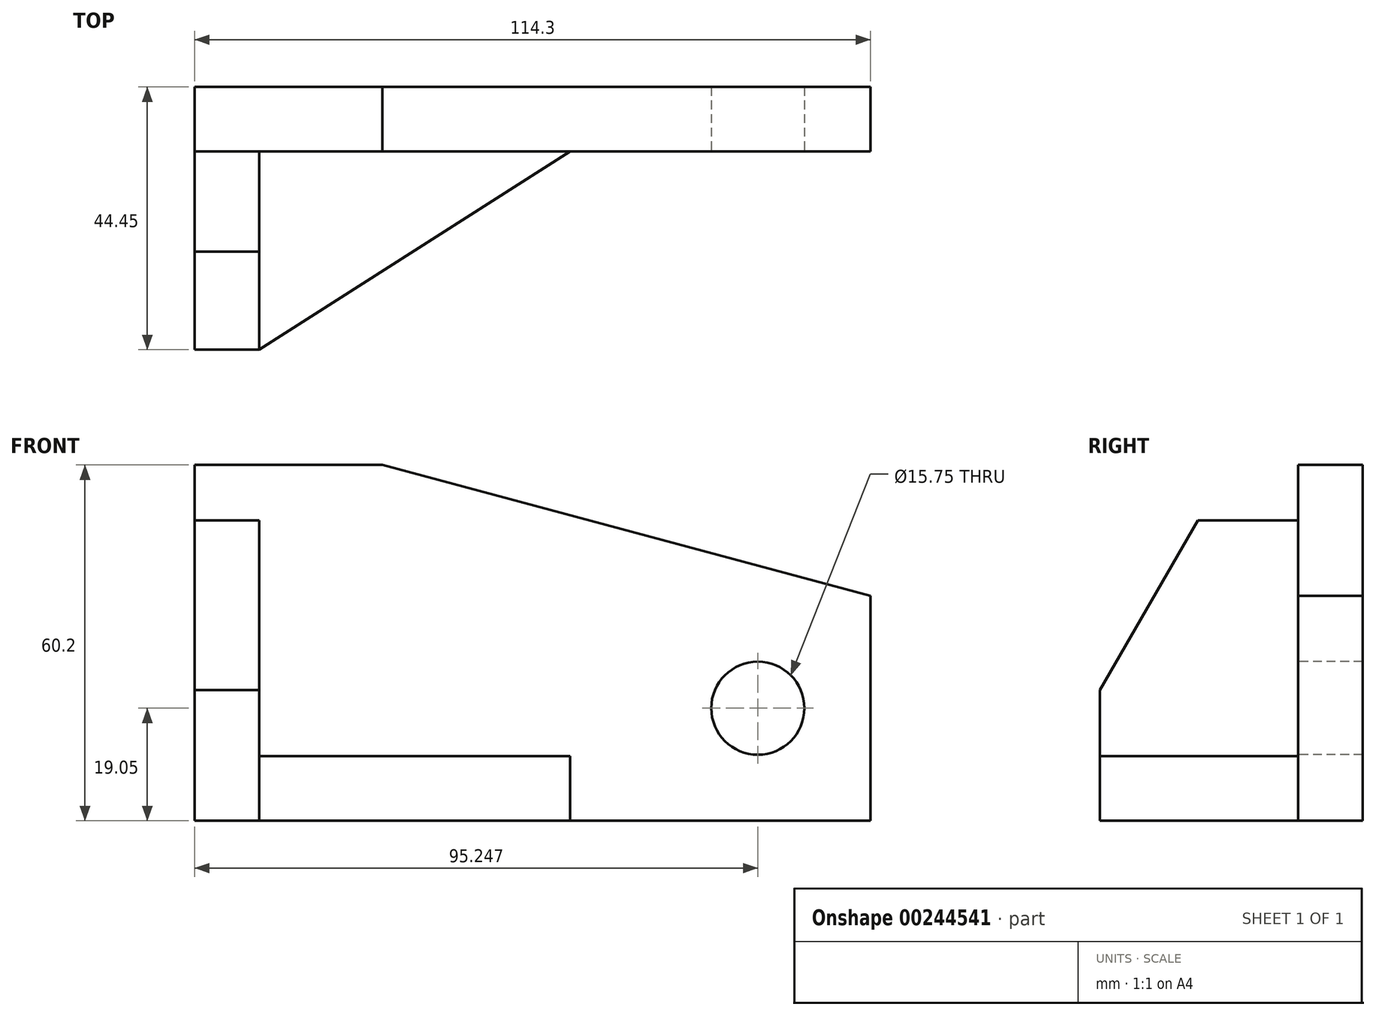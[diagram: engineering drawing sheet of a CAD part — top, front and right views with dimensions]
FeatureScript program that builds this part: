
annotation { "Feature Type Name" : "Feature", "Feature Type Description" : "" }
export const myFeature = defineFeature(function(context is Context, id is Id, definition is map)
    precondition{}
    {
        {
            var Q0;
            Q0=qCreatedBy(makeId("Top.planeOp"),FACE);
            var sketch = newSketch(context, id + "F0", { "sketchPlane" : qUnion([Q0])});
            skLineSegment(sketch, "E0", {"start": v(-76.4, -76.3) * mm, "end": v(-65.48, -76.3) * mm});
            skLineSegment(sketch, "E1", {"start": v(-76.4, -76.3) * mm, "end": v(-12.9, -76.3) * mm});
            skLineSegment(sketch, "E2", {"start": v(-76.4, -76.3) * mm, "end": v(-76.4, -42.77) * mm});
            skLineSegment(sketch, "E3", {"start": v(-76.4, -42.77) * mm, "end": v(-76.4, -31.85) * mm});
            skLineSegment(sketch, "E4", {"start": v(-65.48, -76.3) * mm, "end": v(-65.48, -42.77) * mm});
            skLineSegment(sketch, "E5", {"start": v(-65.48, -42.77) * mm, "end": v(-76.4, -42.77) * mm});
            skLineSegment(sketch, "E6", {"start": v(-65.48, -42.77) * mm, "end": v(-12.9, -42.77) * mm});
            skLineSegment(sketch, "E7", {"start": v(-12.9, -42.77) * mm, "end": v(-65.48, -76.3) * mm});
            skLineSegment(sketch, "E8", {"start": v(-76.4, -31.85) * mm, "end": v(37.9, -31.85) * mm});
            skLineSegment(sketch, "E9", {"start": v(-12.9, -42.77) * mm, "end": v(37.9, -42.77) * mm});
            skLineSegment(sketch, "E10", {"start": v(37.9, -42.77) * mm, "end": v(37.9, -31.85) * mm});
            skSolve(sketch);
        }
        {
            var Q0;
            Q0=makeQuery(id+"F0.imprint","IMPRINT",FACE,{"disambiguationData":[TD([[makeQuery(id+"F0.imprint","IMPRINT",EDGE,{"derivedFrom":sQuery(id+"F0.wireOp",EDGE,"E4")}),-1.0]])]});
            extrude(context, id + "F1", {"entities" : qUnion([Q0]), "depth" : 10.92 * mm});
        }
        {
            var Q0;
            Q0=makeQuery(id+"F0.imprint","IMPRINT",FACE,{"disambiguationData":[TD([[makeQuery(id+"F0.imprint","IMPRINT",EDGE,{"derivedFrom":sQuery(id+"F0.wireOp",EDGE,"E3")}),-1.0]])]});
            extrude(context, id + "F2", {"entities" : qUnion([Q0]), "operationType" : NewBodyOperationType.ADD, "depth" : 60.2 * mm});
        }
        {
            var Q0;
            Q0=makeQuery(id+"F2.opExtrude","SWEPT_FACE",FACE,{"disambiguationData":[OSD([sQuery(id+"F0.wireOp",EDGE,"E5"),sQuery(id+"F0.wireOp",EDGE,"E6"),sQuery(id+"F0.wireOp",EDGE,"E9")])]});
            var sketch = newSketch(context, id + "F3", { "sketchPlane" : qUnion([Q0])});
            skLineSegment(sketch, "E11", {"start": v(-76.4, 60.2) * mm, "end": v(-44.65, 60.2) * mm});
            skLineSegment(sketch, "E12", {"start": v(-44.65, 60.2) * mm, "end": v(37.9, 38.08) * mm});
            skLineSegment(sketch, "E13", {"start": v(-44.65, 60.2) * mm, "end": v(37.9, 60.2) * mm});
            skLineSegment(sketch, "E14", {"start": v(37.9, 60.2) * mm, "end": v(37.9, 38.08) * mm});
            skSolve(sketch);
        }
        {
            var Q0;
            Q0=makeQuery(id+"F3.imprint","IMPRINT",FACE,{"disambiguationData":[TD([[makeQuery(id+"F3.imprint","IMPRINT",EDGE,{"derivedFrom":sQuery(id+"F3.wireOp",EDGE,"E12")}),1.0]])]});
            extrude(context, id + "F4", {"entities" : qUnion([Q0]), "operationType" : NewBodyOperationType.REMOVE, "oppositeDirection" : true, "depth" : 25.4 * mm});
        }
        {
            var Q0;
            {var subQ0=sQuery(id+"F0.wireOp",EDGE,"E2");Q0=makeQuery(id+"F0.imprint","IMPRINT",FACE,{"disambiguationData":[TD([[makeQuery(id+"F0.imprint","IMPRINT",EDGE,{"derivedFrom":subQ0}),-1.0]])]});}
            extrude(context, id + "F5", {"entities" : qUnion([Q0]), "operationType" : NewBodyOperationType.ADD, "depth" : 50.8 * mm});
        }
        {
            var Q0;
            Q0=makeQuery(id+"F5.boolean.opBoolean","MERGE",FACE,{"derivedFrom":[makeQuery(id+"F2.opExtrude","SWEPT_FACE",FACE,{"disambiguationData":[OSD([sQuery(id+"F0.wireOp",EDGE,"E3")])]}),makeQuery(id+"F5.opExtrude","SWEPT_FACE",FACE,{"disambiguationData":[OSD([sQuery(id+"F0.wireOp",EDGE,"E2")])]})]});
            var sketch = newSketch(context, id + "F6", { "sketchPlane" : qUnion([Q0])});
            skPoint(sketch, "E15", {"position": v(76.3, 22.1) * mm});
            skLineSegment(sketch, "E16", {"start": v(76.3, 22.1) * mm, "end": v(59.72, 50.8) * mm});
            skSolve(sketch);
        }
        {
            var Q0;
            Q0 = qSketchRegion(id + "F6", true);
            var Q1;
            {var subQ0=sQuery(id+"F6.wireOp",EDGE,"E16");Q1=makeQuery(id+"F6.imprint","IMPRINT",FACE,{"disambiguationData":[TD([[makeQuery(id+"F6.imprint","IMPRINT",EDGE,{"derivedFrom":subQ0}),-1.0]])]});}
            extrude(context, id + "F7", {"entities" : qUnion([Q0, Q1]), "operationType" : NewBodyOperationType.REMOVE, "oppositeDirection" : true, "depth" : 25.4 * mm});
        }
        {
            var Q0;
            Q0=makeQuery(id+"F2.opExtrude","SWEPT_FACE",FACE,{"disambiguationData":[OSD([sQuery(id+"F0.wireOp",EDGE,"E5"),sQuery(id+"F0.wireOp",EDGE,"E6"),sQuery(id+"F0.wireOp",EDGE,"E9")])]});
            var sketch = newSketch(context, id + "F8", { "sketchPlane" : qUnion([Q0])});
            skLineSegment(sketch, "E17", {"start": v(37.9, 0) * mm, "end": v(18.85, 0) * mm});
            skLineSegment(sketch, "E18", {"start": v(18.85, 0) * mm, "end": v(18.85, 19.05) * mm});
            skCircle(sketch, "E19", {"center": v(18.85, 19.05) * mm, "radius": 7.87 * mm});
            skSolve(sketch);
        }
        {
            var Q0;
            Q0=makeQuery(id+"F8.imprint","IMPRINT",FACE,{"disambiguationData":[TD([[makeQuery(id+"F8.imprint","IMPRINT",EDGE,{"derivedFrom":sQuery(id+"F8.wireOp",EDGE,"E19")}),1.0]])]});
            extrude(context, id + "F9", {"entities" : qUnion([Q0]), "operationType" : NewBodyOperationType.REMOVE, "endBound" : BoundingType.THROUGH_ALL, "oppositeDirection" : true, "depth" : 25.4 * mm});
        }
    });
